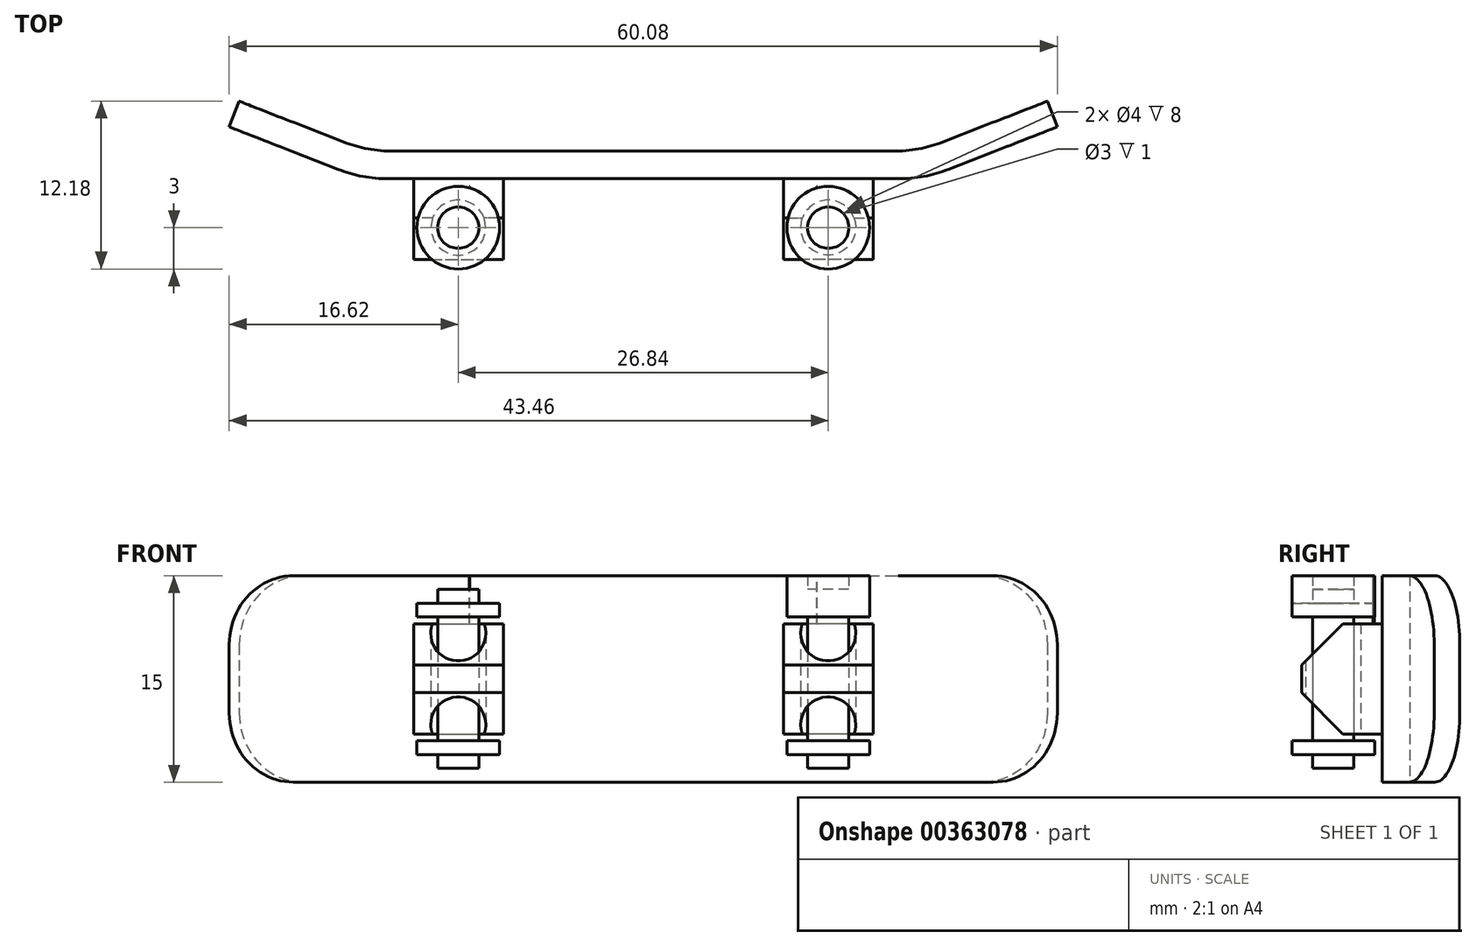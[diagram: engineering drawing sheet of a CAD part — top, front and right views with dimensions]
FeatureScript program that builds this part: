
annotation { "Feature Type Name" : "Feature", "Feature Type Description" : "" }
export const myFeature = defineFeature(function(context is Context, id is Id, definition is map)
    precondition{}
    {
        {
            var Q0;
            Q0=qCreatedBy(makeId("Top.planeOp"),FACE);
            var sketch = newSketch(context, id + "F0", { "sketchPlane" : qUnion([Q0])});
            skLineSegment(sketch, "E0", {"start": v(0, 0) * mm, "end": v(20, 0) * mm});
            skLineSegment(sketch, "E1", {"start": v(20, 0) * mm, "end": v(29.32, 3.63) * mm});
            skLineSegment(sketch, "E2.0", {"start": v(20.38, -2) * mm, "end": v(30.04, 1.77) * mm});
            skLineSegment(sketch, "E2.1", {"start": v(0, -2) * mm, "end": v(20.38, -2) * mm});
            skLineSegment(sketch, "E3", {"start": v(29.32, 3.63) * mm, "end": v(30.04, 1.77) * mm});
            skLineSegment(sketch, "E4", {"start": v(0, 10.06) * mm, "end": v(0, -9.3) * mm, "construction": true});
            skLineSegment(sketch, "E5.MirrorCS", {"start": v(-29.32, 3.63) * mm, "end": v(-30.04, 1.77) * mm});
            skLineSegment(sketch, "E6.MirrorCS", {"start": v(-20, 0) * mm, "end": v(-29.32, 3.63) * mm});
            skLineSegment(sketch, "E7.MirrorCS", {"start": v(-20.38, -2) * mm, "end": v(-30.04, 1.77) * mm});
            skLineSegment(sketch, "E8.MirrorCS", {"start": v(0, 0) * mm, "end": v(-20, 0) * mm});
            skLineSegment(sketch, "E9.MirrorCS", {"start": v(0, -2) * mm, "end": v(-20.38, -2) * mm});
            skSolve(sketch);
        }
        {
            var Q0;
            Q0=makeQuery(id+"F0.imprint","IMPRINT",FACE,{"disambiguationData":[TD([[makeQuery(id+"F0.imprint","IMPRINT",EDGE,{"derivedFrom":sQuery(id+"F0.wireOp",EDGE,"E0")}),-1.0]])]});
            extrude(context, id + "F1", {"entities" : qUnion([Q0]), "endBound" : BoundingType.SYMMETRIC, "depth" : 15 * mm});
        }
        {
            var Q0;
            Q0=makeQuery(id+"F1.opExtrude","CAP_EDGE",EDGE,{"disambiguationData":[OSD([sQuery(id+"F0.wireOp",EDGE,"E3")])],"isStart":false});
            var Q1;
            Q1=makeQuery(id+"F1.opExtrude","CAP_EDGE",EDGE,{"disambiguationData":[OSD([sQuery(id+"F0.wireOp",EDGE,"E3")])],"isStart":true});
            var Q2;
            Q2=makeQuery(id+"F1.opExtrude","CAP_EDGE",EDGE,{"disambiguationData":[OSD([sQuery(id+"F0.wireOp",EDGE,"E5.MirrorCS")])],"isStart":false});
            var Q3;
            Q3=makeQuery(id+"F1.opExtrude","CAP_EDGE",EDGE,{"disambiguationData":[OSD([sQuery(id+"F0.wireOp",EDGE,"E5.MirrorCS")])],"isStart":true});
            fillet(context, id + "F2", {"entities" : qUnion([Q0, Q1, Q2, Q3]), "radius" : 5 * mm, "tangentPropagation" : true, "allowEdgeOverflow" : false});
        }
        {
            var Q0;
            Q0=makeQuery(id+"F1.opExtrude","SWEPT_EDGE",EDGE,{"disambiguationData":[OSD([sQuery(id+"F0.wireOp",EDGE,"E0"),sQuery(id+"F0.wireOp",EDGE,"E1")])]});
            var Q1;
            Q1=makeQuery(id+"F1.opExtrude","SWEPT_EDGE",EDGE,{"disambiguationData":[OSD([sQuery(id+"F0.wireOp",EDGE,"E6.MirrorCS"),sQuery(id+"F0.wireOp",EDGE,"E8.MirrorCS")])]});
            var Q2;
            Q2=makeQuery(id+"F1.opExtrude","SWEPT_EDGE",EDGE,{"disambiguationData":[OSD([sQuery(id+"F0.wireOp",EDGE,"E7.MirrorCS"),sQuery(id+"F0.wireOp",EDGE,"E9.MirrorCS")])]});
            var Q3;
            Q3=makeQuery(id+"F1.opExtrude","SWEPT_EDGE",EDGE,{"disambiguationData":[OSD([sQuery(id+"F0.wireOp",EDGE,"E2.0"),sQuery(id+"F0.wireOp",EDGE,"E2.1")])]});
            fillet(context, id + "F3", {"entities" : qUnion([Q0, Q1, Q2, Q3]), "radius" : 10 * mm, "tangentPropagation" : true, "allowEdgeOverflow" : false});
        }
        {
            var Q0;
            Q0=qCreatedBy(makeId("Top.planeOp"),FACE);
            var sketch = newSketch(context, id + "F4", { "sketchPlane" : qUnion([Q0])});
            skLineSegment(sketch, "E10.bottom", {"start": v(16.67, -2) * mm, "end": v(10.16, -2) * mm});
            skLineSegment(sketch, "E10.top", {"start": v(16.67, -7.85) * mm, "end": v(10.16, -7.85) * mm});
            skLineSegment(sketch, "E10.left", {"start": v(16.67, -2) * mm, "end": v(16.67, -7.85) * mm});
            skLineSegment(sketch, "E10.right", {"start": v(10.16, -2) * mm, "end": v(10.16, -7.85) * mm});
            skCircle(sketch, "E11", {"center": v(13.42, -5.55) * mm, "radius": 2 * mm});
            skPoint(sketch, "E11.centerSnap0", {"position": v(13.42, -7.85) * mm});
            skCircle(sketch, "E12", {"center": v(13.42, -5.55) * mm, "radius": 1.5 * mm});
            skSolve(sketch);
        }
        {
            var Q0;
            Q0=makeQuery(id+"F4.imprint","IMPRINT",FACE,{"disambiguationData":[TD([[makeQuery(id+"F4.imprint","IMPRINT",EDGE,{"derivedFrom":sQuery(id+"F4.wireOp",EDGE,"E10.bottom")}),1.0]])]});
            extrude(context, id + "F5", {"entities" : qUnion([Q0]), "depth" : 4 * mm});
        }
        {
            var Q0;
            Q0=makeQuery(id+"F4.imprint","IMPRINT",FACE,{"disambiguationData":[TD([[makeQuery(id+"F4.imprint","IMPRINT",EDGE,{"derivedFrom":sQuery(id+"F4.wireOp",EDGE,"E12")}),1.0]])]});
            extrude(context, id + "F6", {"entities" : qUnion([Q0]), "endBound" : BoundingType.SYMMETRIC, "depth" : 13 * mm});
        }
        {
            var Q0;
            Q0=makeQuery(id+"F5.opExtrude","CAP_EDGE",EDGE,{"disambiguationData":[OSD([sQuery(id+"F4.wireOp",EDGE,"E10.top")])],"isStart":false});
            chamfer(context, id + "F7", {"entities" : qUnion([Q0]), "width" : 3 * mm, "tangentPropagation" : true});
        }
        {
            var Q0;
            Q0=makeQuery(id+"F6.opExtrude","CAP_FACE",FACE,{"disambiguationData":[OSD([sQuery(id+"F4.wireOp",EDGE,"E12")])],"isStart":false});
            var sketch = newSketch(context, id + "F8", { "sketchPlane" : qUnion([Q0])});
            skCircle(sketch, "E13", {"center": v(13.42, -5.55) * mm, "radius": 3 * mm});
            skSolve(sketch);
        }
        {
            var Q0;
            Q0=makeQuery(id+"F8.imprint","IMPRINT",FACE,{"disambiguationData":[TD([[makeQuery(id+"F8.imprint","IMPRINT",EDGE,{"derivedFrom":sQuery(id+"F8.wireOp",EDGE,"E13")}),1.0]])]});
            extrude(context, id + "F9", {"entities" : qUnion([Q0]), "endBound" : BoundingType.SYMMETRIC, "depth" : 2 * mm});
        }
        {
            var Q0;
            Q0=makeQuery(id+"F9.opExtrude","CAP_FACE",FACE,{"disambiguationData":[OSD([sQuery(id+"F4.wireOp",EDGE,"E12"),sQuery(id+"F8.wireOp",EDGE,"E13")])],"isStart":true});
            extrude(context, id + "F10", {"entities" : qUnion([Q0]), "depth" : 1 * mm});
        }
        {
            var Q0;
            Q0=makeQuery(id+"F5.opExtrude","SWEPT_BODY",BODY,{"disambiguationData":[OSD([sQuery(id+"F4.wireOp",EDGE,"E10.bottom"),sQuery(id+"F4.wireOp",EDGE,"E10.top"),sQuery(id+"F4.wireOp",EDGE,"E10.left"),sQuery(id+"F4.wireOp",EDGE,"E10.right"),sQuery(id+"F4.wireOp",EDGE,"E11")])]});
            var Q1;
            Q1=makeQuery(id+"F10.opExtrude","SWEPT_BODY",BODY,{"disambiguationData":[OSD([sQuery(id+"F4.wireOp",EDGE,"E12"),sQuery(id+"F8.wireOp",EDGE,"E13")])]});
            var Q2;
            Q2=qCreatedBy(makeId("Top.planeOp"),FACE);
            mirror(context, id + "F11", {"entities" : qUnion([Q0, Q1]), "mirrorPlane" : qUnion([Q2])});
        }
        {
            var Q0;
            Q0=makeQuery(id+"F11.opPattern","COPY",BODY,{"derivedFrom":makeQuery(id+"F10.opExtrude","SWEPT_BODY",BODY,{"disambiguationData":[OSD([sQuery(id+"F4.wireOp",EDGE,"E12"),sQuery(id+"F8.wireOp",EDGE,"E13")])]}),"instanceName":"1"});
            var Q1;
            Q1=makeQuery(id+"F11.opPattern","COPY",BODY,{"derivedFrom":makeQuery(id+"F5.opExtrude","SWEPT_BODY",BODY,{"disambiguationData":[OSD([sQuery(id+"F4.wireOp",EDGE,"E10.bottom"),sQuery(id+"F4.wireOp",EDGE,"E10.top"),sQuery(id+"F4.wireOp",EDGE,"E10.left"),sQuery(id+"F4.wireOp",EDGE,"E10.right"),sQuery(id+"F4.wireOp",EDGE,"E11")])]}),"instanceName":"1"});
            var Q2;
            Q2=makeQuery(id+"F6.opExtrude","SWEPT_BODY",BODY,{"disambiguationData":[OSD([sQuery(id+"F4.wireOp",EDGE,"E12")])]});
            var Q3;
            Q3=makeQuery(id+"F5.opExtrude","SWEPT_BODY",BODY,{"disambiguationData":[OSD([sQuery(id+"F4.wireOp",EDGE,"E10.bottom"),sQuery(id+"F4.wireOp",EDGE,"E10.top"),sQuery(id+"F4.wireOp",EDGE,"E10.left"),sQuery(id+"F4.wireOp",EDGE,"E10.right"),sQuery(id+"F4.wireOp",EDGE,"E11")])]});
            var Q4;
            Q4=makeQuery(id+"F10.opExtrude","SWEPT_BODY",BODY,{"disambiguationData":[OSD([sQuery(id+"F4.wireOp",EDGE,"E12"),sQuery(id+"F8.wireOp",EDGE,"E13")])]});
            var Q5;
            Q5=qCreatedBy(makeId("Right.planeOp"),FACE);
            mirror(context, id + "F12", {"operationType" : NewBodyOperationType.ADD, "entities" : qUnion([Q0, Q1, Q2, Q3, Q4]), "mirrorPlane" : qUnion([Q5])});
        }
        {
            var Q0;
            Q0=makeQuery(id+"F9.opExtrude","CAP_FACE",FACE,{"disambiguationData":[OSD([sQuery(id+"F4.wireOp",EDGE,"E12"),sQuery(id+"F8.wireOp",EDGE,"E13")])],"isStart":false});
            var sketch = newSketch(context, id + "F13", { "sketchPlane" : qUnion([Q0])});
            skLineSegment(sketch, "E14.bottom", {"start": v(12.6, -2.56) * mm, "end": v(12.61, -2.56) * mm});
            skLineSegment(sketch, "E14.top", {"start": v(12.6, -2.66) * mm, "end": v(12.61, -2.66) * mm});
            skLineSegment(sketch, "E14.left", {"start": v(12.61, -2.56) * mm, "end": v(12.61, -2.66) * mm});
            skLineSegment(sketch, "E14.right", {"start": v(12.6, -2.56) * mm, "end": v(12.6, -2.66) * mm});
            skSolve(sketch);
        }
        {
            var Q0;
            Q0=makeQuery(id+"F13.imprint","IMPRINT",FACE,{"disambiguationData":[TD([[makeQuery(id+"F13.imprint","IMPRINT",EDGE,{"derivedFrom":sQuery(id+"F13.wireOp",EDGE,"E14.bottom")}),-1.0]])]});
            extrude(context, id + "F14", {"entities" : qUnion([Q0]), "oppositeDirection" : true, "depth" : 5 * mm});
        }
        {
            var Q0;
            Q0=makeQuery(id+"F14.opExtrude","SWEPT_BODY",BODY,{"disambiguationData":[OSD([sQuery(id+"F13.wireOp",EDGE,"E14.bottom"),sQuery(id+"F13.wireOp",EDGE,"E14.top"),sQuery(id+"F13.wireOp",EDGE,"E14.left"),sQuery(id+"F13.wireOp",EDGE,"E14.right")])]});
            var Q1;
            Q1=qCreatedBy(makeId("Right.planeOp"),FACE);
            mirror(context, id + "F15", {"operationType" : NewBodyOperationType.ADD, "entities" : qUnion([Q0]), "mirrorPlane" : qUnion([Q1])});
        }
        {
            var Q0;
            Q0=makeQuery(id+"F12.opPattern","COPY",BODY,{"derivedFrom":makeQuery(id+"F6.opExtrude","SWEPT_BODY",BODY,{"disambiguationData":[OSD([sQuery(id+"F4.wireOp",EDGE,"E12")])]}),"instanceName":"1"});
            var Q1;
            Q1=makeQuery(id+"F1.opExtrude","SWEPT_BODY",BODY,{"disambiguationData":[OSD([sQuery(id+"F0.wireOp",EDGE,"E0"),sQuery(id+"F0.wireOp",EDGE,"E1"),sQuery(id+"F0.wireOp",EDGE,"E2.0"),sQuery(id+"F0.wireOp",EDGE,"E2.1"),sQuery(id+"F0.wireOp",EDGE,"E3"),sQuery(id+"F0.wireOp",EDGE,"E5.MirrorCS"),sQuery(id+"F0.wireOp",EDGE,"E6.MirrorCS"),sQuery(id+"F0.wireOp",EDGE,"E7.MirrorCS"),sQuery(id+"F0.wireOp",EDGE,"E8.MirrorCS"),sQuery(id+"F0.wireOp",EDGE,"E9.MirrorCS")])]});
            var Q2;
            Q2=makeQuery(id+"F6.opExtrude","SWEPT_BODY",BODY,{"disambiguationData":[OSD([sQuery(id+"F4.wireOp",EDGE,"E12")])]});
            booleanBodies(context, id + "F16", {"operationType" : BooleanOperationType.UNION, "tools" : qUnion([Q0, Q1, Q2])});
        }
    });
